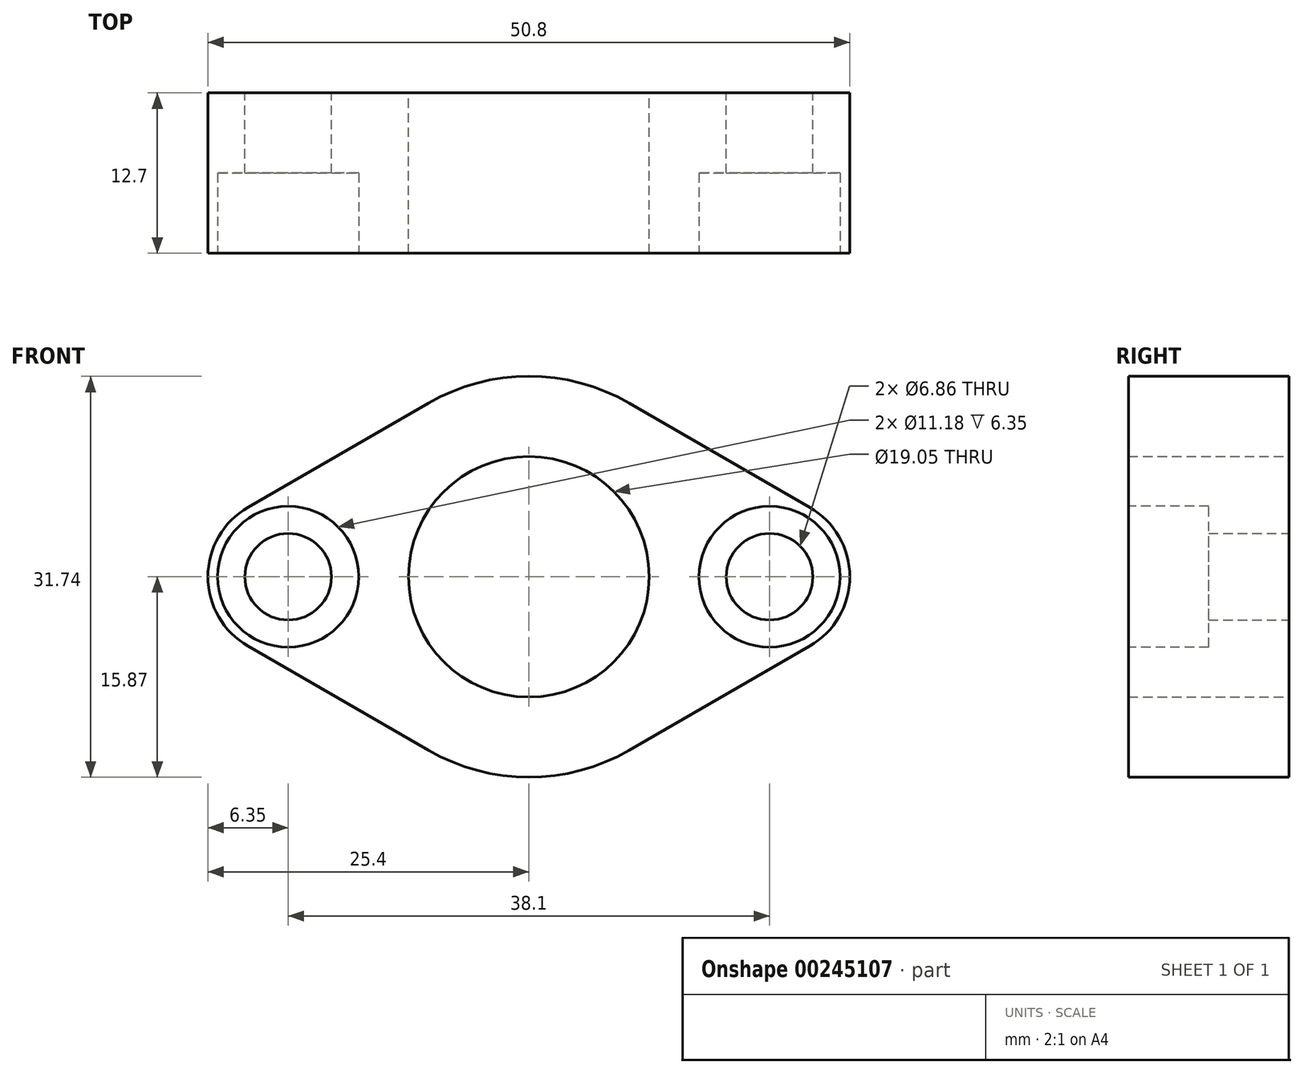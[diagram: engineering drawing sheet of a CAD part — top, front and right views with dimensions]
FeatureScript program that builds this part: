
annotation { "Feature Type Name" : "Feature", "Feature Type Description" : "" }
export const myFeature = defineFeature(function(context is Context, id is Id, definition is map)
    precondition{}
    {
        {
            var Q0;
            Q0=qCreatedBy(makeId("Front.planeOp"),FACE);
            var sketch = newSketch(context, id + "F0", { "sketchPlane" : qUnion([Q0])});
            skCircle(sketch, "E0", {"center": v(0, 0) * mm, "radius": 9.53 * mm});
            skCircle(sketch, "E1", {"center": v(-19.05, 0) * mm, "radius": 3.43 * mm});
            skCircle(sketch, "E2", {"center": v(19.05, 0) * mm, "radius": 3.43 * mm});
            skPoint(sketch, "E3.end.orphan", {"position": v(0, -10.1) * mm});
            skPoint(sketch, "E4.start.orphan", {"position": v(0, -10.08) * mm});
            skArc(sketch, "E5", {"start": v(-22.23, 5.5) * mm, "mid": v(-25.4, 0) * mm, "end": v(-22.23, -5.5) * mm});
            skArc(sketch, "E6", {"start": v(-7.94, -13.75) * mm, "mid": v(0, -15.88) * mm, "end": v(7.94, -13.75) * mm});
            skArc(sketch, "E7", {"start": v(22.23, -5.5) * mm, "mid": v(25.4, 0) * mm, "end": v(22.22, 5.5) * mm});
            skLineSegment(sketch, "E8", {"start": v(-22.23, 5.5) * mm, "end": v(-7.94, 13.75) * mm});
            skLineSegment(sketch, "E9", {"start": v(7.94, 13.75) * mm, "end": v(22.22, 5.5) * mm});
            skLineSegment(sketch, "E10", {"start": v(-22.23, -5.5) * mm, "end": v(-7.94, -13.75) * mm});
            skLineSegment(sketch, "E11", {"start": v(7.94, -13.75) * mm, "end": v(22.22, -5.5) * mm});
            skPoint(sketch, "E12.orphan", {"position": v(0, -18.33) * mm});
            skArc(sketch, "E13.trimOffspring", {"start": v(7.94, 13.75) * mm, "mid": v(0, 15.88) * mm, "end": v(-7.94, 13.75) * mm});
            skSolve(sketch);
        }
        {
            var Q0;
            Q0=makeQuery(id+"F0.imprint","IMPRINT",FACE,{"disambiguationData":[TD([[makeQuery(id+"F0.imprint","IMPRINT",EDGE,{"derivedFrom":sQuery(id+"F0.wireOp",EDGE,"E0")}),-1.0]])]});
            extrude(context, id + "F1", {"entities" : qUnion([Q0]), "depth" : 12.7 * mm});
        }
        {
            var Q0;
            Q0=makeQuery(id+"F1.opExtrude","CAP_FACE",FACE,{"disambiguationData":[OSD([sQuery(id+"F0.wireOp",EDGE,"E0"),sQuery(id+"F0.wireOp",EDGE,"E1"),sQuery(id+"F0.wireOp",EDGE,"E2"),sQuery(id+"F0.wireOp",EDGE,"E5"),sQuery(id+"F0.wireOp",EDGE,"E6"),sQuery(id+"F0.wireOp",EDGE,"E7"),sQuery(id+"F0.wireOp",EDGE,"E8"),sQuery(id+"F0.wireOp",EDGE,"E9"),sQuery(id+"F0.wireOp",EDGE,"E10"),sQuery(id+"F0.wireOp",EDGE,"E11"),sQuery(id+"F0.wireOp",EDGE,"E13.trimOffspring")])],"isStart":false});
            var sketch = newSketch(context, id + "F2", { "sketchPlane" : qUnion([Q0])});
            skCircle(sketch, "E14", {"center": v(-19.05, 0) * mm, "radius": 5.59 * mm});
            skCircle(sketch, "E15", {"center": v(19.05, 0) * mm, "radius": 5.59 * mm});
            skSolve(sketch);
        }
        {
            var Q0;
            Q0=makeQuery(id+"F2.imprint","IMPRINT",FACE,{"disambiguationData":[TD([[makeQuery(id+"F2.imprint","IMPRINT",EDGE,{"derivedFrom":sQuery(id+"F2.wireOp",EDGE,"E14")}),1.0]])]});
            var Q1;
            Q1=makeQuery(id+"F2.imprint","IMPRINT",FACE,{"disambiguationData":[TD([[makeQuery(id+"F2.imprint","IMPRINT",EDGE,{"derivedFrom":sQuery(id+"F2.wireOp",EDGE,"E15")}),1.0]])]});
            extrude(context, id + "F3", {"entities" : qUnion([Q0, Q1]), "operationType" : NewBodyOperationType.REMOVE, "oppositeDirection" : true, "depth" : 6.35 * mm});
        }
    });
